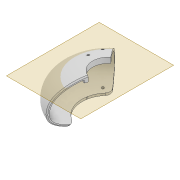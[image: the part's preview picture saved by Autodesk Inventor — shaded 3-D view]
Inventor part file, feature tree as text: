
AUTODESK INVENTOR PART (.ipt)
format: ipt  version: 2022 (Build 260153000, 153)  size: 434,688 bytes
history: native  units: mm
features: sketch x6, extrude x5, plane x2, revolve x1, chamfer x1, fillet x1, projected_geometry x1
ambient origin geometry x8: Origin, YZ Plane, XZ Plane, XY Plane, X Axis, Y Axis, Z Axis, Center Point
bodies: Solid1 (feature_tree)
feature tree (17):
  revolve  "Revolution1"  [1 undecoded]
  extrude  "Extrusion1"  Depth=27.925268mm
  extrude  "Extrusion2"  Depth=20.0mm TaperAngle=0.0deg
  extrude  "Extrusion3"  Depth=2.1mm
  plane  "Work Plane2"
  extrude  "Extrusion7"  Depth=4.5mm
  plane  "Work Plane3"
  extrude  "Extrusion8"  Depth=5.0mm
  chamfer  "Chamfer3"  Distance=100.0mm
  fillet  "Fillet1"  Radius=6.981317mm
  sketch  "Sketch1"  dims[d2=45.0mm d3=40.0mm]
  sketch  "Sketch2"  dims[d4=2.0mm d5=27.925268mm]
  sketch  "Sketch3"  dims[d6=50.0mm d7=20.0mm d8=0.0mm]
  sketch  "Sketch4"  dims[d9=2.1mm d10=2.1mm]
  projected_geometry  "Projected Loop1"
  sketch  "Sketch8"  dims[d11=23.6mm d12=4.5mm]
  sketch  "Sketch9"  dims[d13=23.6mm d14=18.0mm d15=100.0mm d16=0.0mm d17=6.981317mm d18=100.0mm d19=0.0mm d38=30.0mm d39=30.0mm d40=20.0mm d41=0.0mm d42=34.0mm d43=3.0mm d44=4.0mm d45=0.0mm d46=1.0mm d47=2.0mm d48=45.0deg d49=5.0mm]
note: 1 required parameter value undecoded (feature->parameter linkage not recoverable at this tier; creation-order binding heuristic only, values carry confidence <= 0.55)
